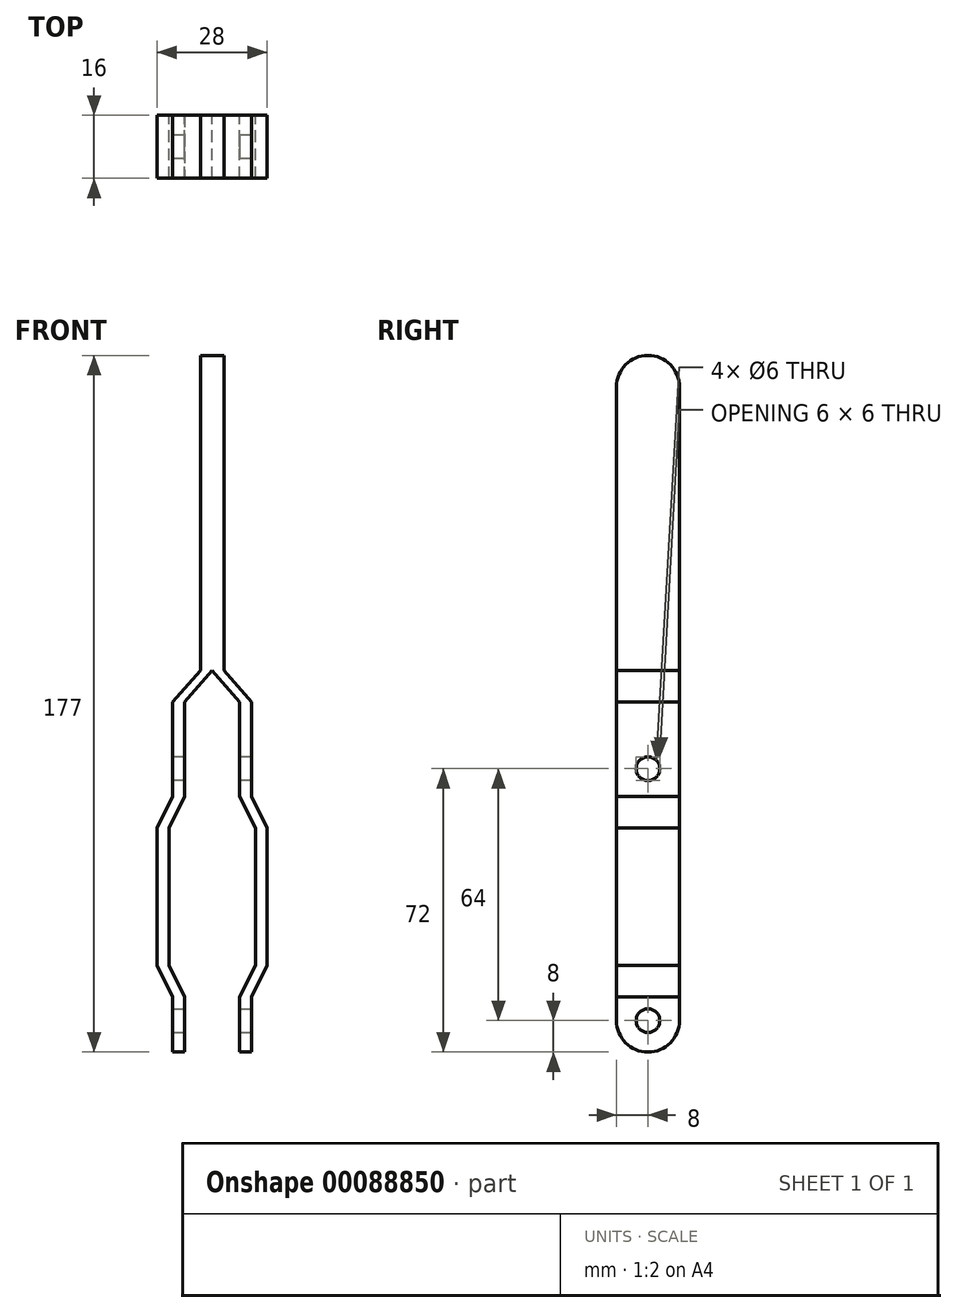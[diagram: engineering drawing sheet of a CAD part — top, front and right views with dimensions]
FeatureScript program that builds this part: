
annotation { "Feature Type Name" : "Feature", "Feature Type Description" : "" }
export const myFeature = defineFeature(function(context is Context, id is Id, definition is map)
    precondition{}
    {
        {
            var Q0;
            Q0=qCreatedBy(makeId("Front.planeOp"),FACE);
            var sketch = newSketch(context, id + "F0", { "sketchPlane" : qUnion([Q0])});
            skLineSegment(sketch, "E0.bottom", {"start": v(-3, 72) * mm, "end": v(3, 72) * mm});
            skLineSegment(sketch, "E0.top", {"start": v(-3, 0) * mm, "end": v(3, 0) * mm});
            skLineSegment(sketch, "E0.left", {"start": v(-3, 72) * mm, "end": v(-3, 0) * mm});
            skLineSegment(sketch, "E0.right", {"start": v(3, 72) * mm, "end": v(3, 0) * mm});
            skLineSegment(sketch, "E1", {"start": v(-10, -8) * mm, "end": v(-10, -32) * mm});
            skLineSegment(sketch, "E2", {"start": v(-7, -8) * mm, "end": v(-7, -32) * mm});
            skLineSegment(sketch, "E3.MirrorCS", {"start": v(7, -8) * mm, "end": v(7, -32) * mm});
            skLineSegment(sketch, "E4.MirrorCS", {"start": v(10, -8) * mm, "end": v(10, -32) * mm});
            skLineSegment(sketch, "E5", {"start": v(-10, -8) * mm, "end": v(-3, 0) * mm});
            skLineSegment(sketch, "E6.MirrorCS", {"start": v(10, -8) * mm, "end": v(3, 0) * mm});
            skLineSegment(sketch, "E7", {"start": v(-7, -8) * mm, "end": v(0, 0) * mm});
            skLineSegment(sketch, "E8", {"start": v(0, 0) * mm, "end": v(7, -8) * mm});
            skLineSegment(sketch, "E9", {"start": v(-10, -32) * mm, "end": v(-14, -40) * mm});
            skLineSegment(sketch, "E10", {"start": v(-7, -32) * mm, "end": v(-11, -40) * mm});
            skLineSegment(sketch, "E11", {"start": v(-7, -32) * mm, "end": v(-7, -40) * mm, "construction": true});
            skLineSegment(sketch, "E12", {"start": v(-7, -40) * mm, "end": v(-11, -40) * mm, "construction": true});
            skLineSegment(sketch, "E13.MirrorCS", {"start": v(7, -32) * mm, "end": v(11, -40) * mm});
            skLineSegment(sketch, "E14.MirrorCS", {"start": v(10, -32) * mm, "end": v(14, -40) * mm});
            skLineSegment(sketch, "E15", {"start": v(-14, -40) * mm, "end": v(-14, -75) * mm});
            skLineSegment(sketch, "E16", {"start": v(-11, -40) * mm, "end": v(-11, -75) * mm});
            skLineSegment(sketch, "E17.MirrorCS", {"start": v(11, -40) * mm, "end": v(11, -75) * mm});
            skLineSegment(sketch, "E18.MirrorCS", {"start": v(14, -40) * mm, "end": v(14, -75) * mm});
            skLineSegment(sketch, "E19", {"start": v(-14, -57.5) * mm, "end": v(-11, -57.5) * mm, "construction": true});
            skLineSegment(sketch, "E20.MirrorCS", {"start": v(-10, -83) * mm, "end": v(-14, -75) * mm});
            skLineSegment(sketch, "E21.MirrorCS", {"start": v(-7, -83) * mm, "end": v(-11, -75) * mm});
            skLineSegment(sketch, "E22.MirrorCS", {"start": v(7, -83) * mm, "end": v(11, -75) * mm});
            skLineSegment(sketch, "E23.MirrorCS", {"start": v(10, -83) * mm, "end": v(14, -75) * mm});
            skLineSegment(sketch, "E24", {"start": v(-10, -83) * mm, "end": v(-10, -89) * mm});
            skLineSegment(sketch, "E25", {"start": v(-7, -83) * mm, "end": v(-7, -89) * mm});
            skLineSegment(sketch, "E26.MirrorCS", {"start": v(7, -83) * mm, "end": v(7, -89) * mm});
            skLineSegment(sketch, "E27.MirrorCS", {"start": v(10, -83) * mm, "end": v(10, -89) * mm});
            skLineSegment(sketch, "E28", {"start": v(-10, -89) * mm, "end": v(-7, -89) * mm});
            skLineSegment(sketch, "E29", {"start": v(7, -89) * mm, "end": v(10, -89) * mm});
            skLineSegment(sketch, "E30", {"start": v(-7, -32) * mm, "end": v(7, -32) * mm, "construction": true});
            skSolve(sketch);
        }
        {
            var Q0;
            Q0=makeQuery(id+"F0.imprint","IMPRINT",FACE,{"disambiguationData":[TD([[makeQuery(id+"F0.imprint","IMPRINT",EDGE,{"derivedFrom":sQuery(id+"F0.wireOp",EDGE,"E0.bottom")}),-1.0]])]});
            var Q1;
            Q1=makeQuery(id+"F0.imprint","IMPRINT",FACE,{"disambiguationData":[TD([[makeQuery(id+"F0.imprint","IMPRINT",EDGE,{"derivedFrom":sQuery(id+"F0.wireOp",EDGE,"E1")}),1.0]])]});
            var Q2;
            Q2=makeQuery(id+"F0.imprint","IMPRINT",FACE,{"disambiguationData":[TD([[makeQuery(id+"F0.imprint","IMPRINT",EDGE,{"derivedFrom":sQuery(id+"F0.wireOp",EDGE,"E3.MirrorCS")}),1.0]])]});
            extrude(context, id + "F1", {"entities" : qUnion([Q0, Q1, Q2]), "depth" : 16 * mm});
        }
        {
            var Q0;
            Q0=makeQuery(id+"F1.opExtrude","SWEPT_FACE",FACE,{"disambiguationData":[OSD([sQuery(id+"F0.wireOp",EDGE,"E1")])]});
            var sketch = newSketch(context, id + "F2", { "sketchPlane" : qUnion([Q0])});
            skCircle(sketch, "E31", {"center": v(8, -25) * mm, "radius": 3 * mm});
            skLineSegment(sketch, "E32", {"start": v(8, -32) * mm, "end": v(8, -25) * mm, "construction": true});
            skSolve(sketch);
        }
        {
            var Q0;
            Q0=makeQuery(id+"F2.imprint","IMPRINT",FACE,{"disambiguationData":[TD([[makeQuery(id+"F2.imprint","IMPRINT",EDGE,{"derivedFrom":sQuery(id+"F2.wireOp",EDGE,"E31")}),1.0]])]});
            extrude(context, id + "F3", {"entities" : qUnion([Q0]), "operationType" : NewBodyOperationType.REMOVE, "oppositeDirection" : true, "depth" : 20 * mm});
        }
        {
            var Q0;
            Q0=makeQuery(id+"F1.opExtrude","SWEPT_FACE",FACE,{"disambiguationData":[OSD([sQuery(id+"F0.wireOp",EDGE,"E0.left")])]});
            var sketch = newSketch(context, id + "F4", { "sketchPlane" : qUnion([Q0])});
            skArc(sketch, "E33", {"start": v(16, 72) * mm, "mid": v(8, 80) * mm, "end": v(0, 72) * mm});
            skSolve(sketch);
        }
        {
            var Q0;
            Q0=makeQuery(id+"F4.imprint","IMPRINT",FACE,{"disambiguationData":[TD([[makeQuery(id+"F4.imprint","IMPRINT",EDGE,{"derivedFrom":sQuery(id+"F4.wireOp",EDGE,"E33")}),1.0]])]});
            extrude(context, id + "F5", {"entities" : qUnion([Q0]), "operationType" : NewBodyOperationType.ADD, "oppositeDirection" : true, "depth" : 6 * mm});
        }
        {
            var Q0;
            Q0=makeQuery(id+"F1.opExtrude","SWEPT_FACE",FACE,{"disambiguationData":[OSD([sQuery(id+"F0.wireOp",EDGE,"E24")])]});
            var sketch = newSketch(context, id + "F6", { "sketchPlane" : qUnion([Q0])});
            skArc(sketch, "E34", {"start": v(0, -89) * mm, "mid": v(8, -97) * mm, "end": v(16, -89) * mm});
            skSolve(sketch);
        }
        {
            var Q0;
            Q0=makeQuery(id+"F6.imprint","IMPRINT",FACE,{"disambiguationData":[TD([[makeQuery(id+"F6.imprint","IMPRINT",EDGE,{"derivedFrom":sQuery(id+"F6.wireOp",EDGE,"E34")}),1.0]])]});
            extrude(context, id + "F7", {"entities" : qUnion([Q0]), "operationType" : NewBodyOperationType.ADD, "oppositeDirection" : true, "depth" : 3 * mm});
        }
        {
            var Q0;
            Q0=makeQuery(id+"F1.opExtrude","SWEPT_FACE",FACE,{"disambiguationData":[OSD([sQuery(id+"F0.wireOp",EDGE,"E27.MirrorCS")])]});
            var sketch = newSketch(context, id + "F8", { "sketchPlane" : qUnion([Q0])});
            skArc(sketch, "E35", {"start": v(-16, -89) * mm, "mid": v(-8, -97) * mm, "end": v(0, -89) * mm});
            skCircle(sketch, "E36", {"center": v(-8, -89) * mm, "radius": 3 * mm});
            skSolve(sketch);
        }
        {
            var Q0;
            Q0 = qSketchRegion(id + "F8", true);
            var Q1;
            Q1=makeQuery(id+"F8.imprint","IMPRINT",FACE,{"disambiguationData":[TD([[makeQuery(id+"F8.imprint","IMPRINT",EDGE,{"derivedFrom":sQuery(id+"F8.wireOp",EDGE,"E35")}),1.0]])]});
            extrude(context, id + "F9", {"entities" : qUnion([Q0, Q1]), "operationType" : NewBodyOperationType.ADD, "oppositeDirection" : true, "depth" : 3 * mm});
        }
        {
            var Q0;
            Q0 = qSketchRegion(id + "F8", true);
            extrude(context, id + "F10", {"entities" : qUnion([Q0]), "operationType" : NewBodyOperationType.REMOVE, "oppositeDirection" : true, "depth" : 20 * mm});
        }
    });
